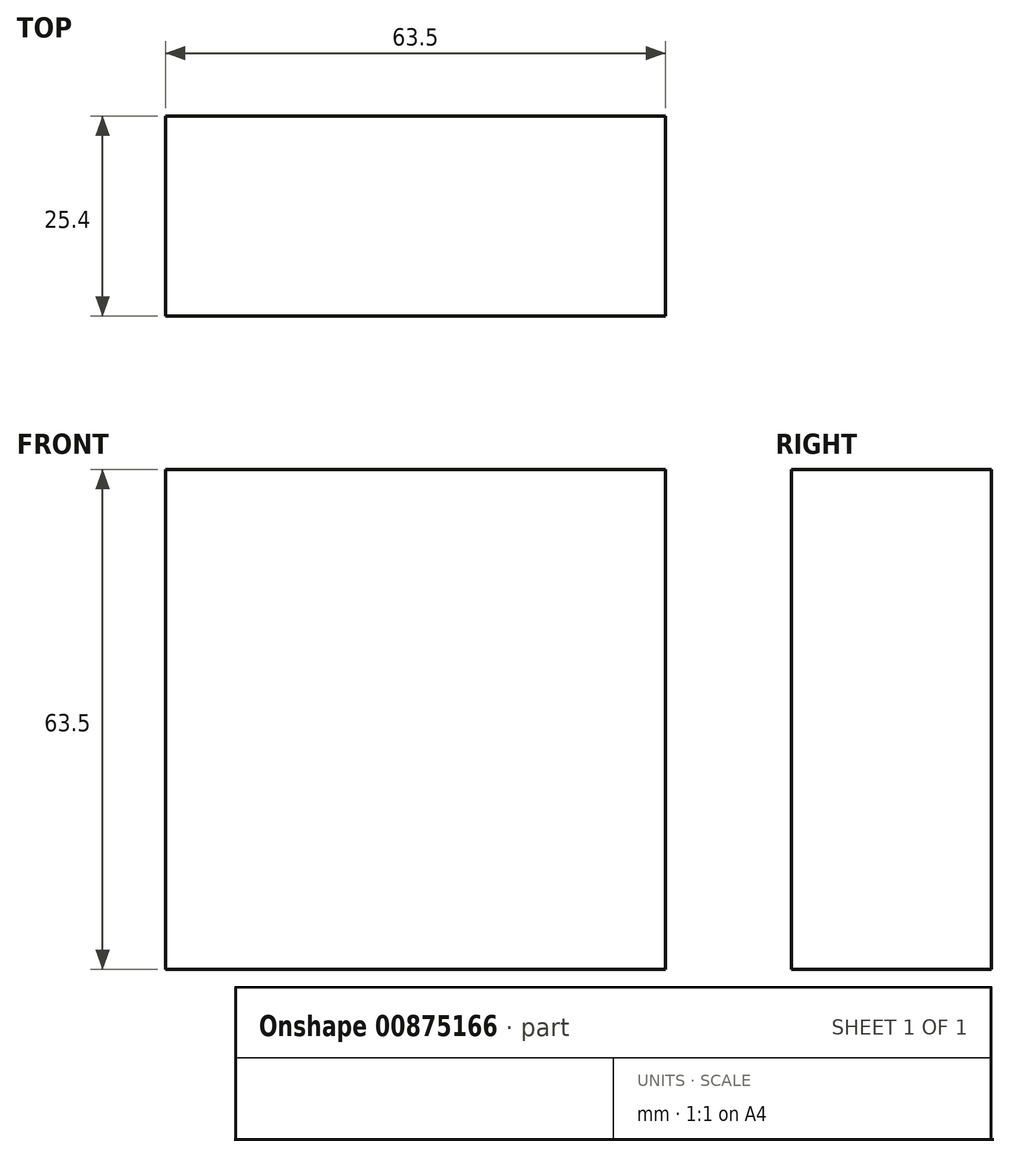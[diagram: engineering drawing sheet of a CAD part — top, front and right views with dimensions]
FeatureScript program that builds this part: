
annotation { "Feature Type Name" : "Feature", "Feature Type Description" : "" }
export const myFeature = defineFeature(function(context is Context, id is Id, definition is map)
    precondition{}
    {
        {
            var Q0;
            Q0=qCreatedBy(makeId("Front.planeOp"),FACE);
            var sketch = newSketch(context, id + "F0", { "sketchPlane" : qUnion([Q0])});
            skLineSegment(sketch, "E0.bottom", {"start": v(-164.57, 68.12) * mm, "end": v(-101.07, 68.12) * mm});
            skLineSegment(sketch, "E0.top", {"start": v(-164.57, 4.62) * mm, "end": v(-101.07, 4.62) * mm});
            skLineSegment(sketch, "E0.left", {"start": v(-164.57, 68.12) * mm, "end": v(-164.57, 4.62) * mm});
            skLineSegment(sketch, "E0.right", {"start": v(-101.07, 68.12) * mm, "end": v(-101.07, 4.62) * mm});
            skSolve(sketch);
        }
        {
            var Q0;
            Q0=makeQuery(id+"F0.imprint","IMPRINT",FACE,{"disambiguationData":[TD([[makeQuery(id+"F0.imprint","IMPRINT",EDGE,{"derivedFrom":sQuery(id+"F0.wireOp",EDGE,"E0.bottom")}),-1.0]])]});
            extrude(context, id + "F1", {"entities" : qUnion([Q0]), "depth" : 1498.6 * mm, "offsetDistance" : 25.4 * mm});
        }
        {
            var Q0;
            Q0=makeQuery(id+"F1.opExtrude","CAP_FACE",FACE,{"disambiguationData":[OSD([sQuery(id+"F0.wireOp",EDGE,"E0.bottom"),sQuery(id+"F0.wireOp",EDGE,"E0.top"),sQuery(id+"F0.wireOp",EDGE,"E0.left"),sQuery(id+"F0.wireOp",EDGE,"E0.right")])],"isStart":true});
            extrude(context, id + "F2", {"entities" : qUnion([Q0]), "operationType" : NewBodyOperationType.REMOVE, "oppositeDirection" : true, "depth" : 1092.2 * mm, "offsetDistance" : 25.4 * mm});
        }
        {
            var Q0;
            Q0=makeQuery(id+"F2.boolean.opBoolean","COPY",FACE,{"derivedFrom":makeQuery(id+"F2.opExtrude","CAP_FACE",FACE,{"disambiguationData":[OSD([sQuery(id+"F0.wireOp",EDGE,"E0.bottom"),sQuery(id+"F0.wireOp",EDGE,"E0.top"),sQuery(id+"F0.wireOp",EDGE,"E0.left"),sQuery(id+"F0.wireOp",EDGE,"E0.right")])],"isStart":false})});
            extrude(context, id + "F3", {"entities" : qUnion([Q0]), "operationType" : NewBodyOperationType.REMOVE, "oppositeDirection" : true, "depth" : 203.2 * mm, "offsetDistance" : 25.4 * mm});
        }
        {
            var Q0;
            Q0=makeQuery(id+"F1.opExtrude","CAP_FACE",FACE,{"disambiguationData":[OSD([sQuery(id+"F0.wireOp",EDGE,"E0.bottom"),sQuery(id+"F0.wireOp",EDGE,"E0.top"),sQuery(id+"F0.wireOp",EDGE,"E0.left"),sQuery(id+"F0.wireOp",EDGE,"E0.right")])],"isStart":false});
            extrude(context, id + "F4", {"entities" : qUnion([Q0]), "operationType" : NewBodyOperationType.REMOVE, "oppositeDirection" : true, "depth" : 177.8 * mm, "offsetDistance" : 25.4 * mm});
        }
    });
